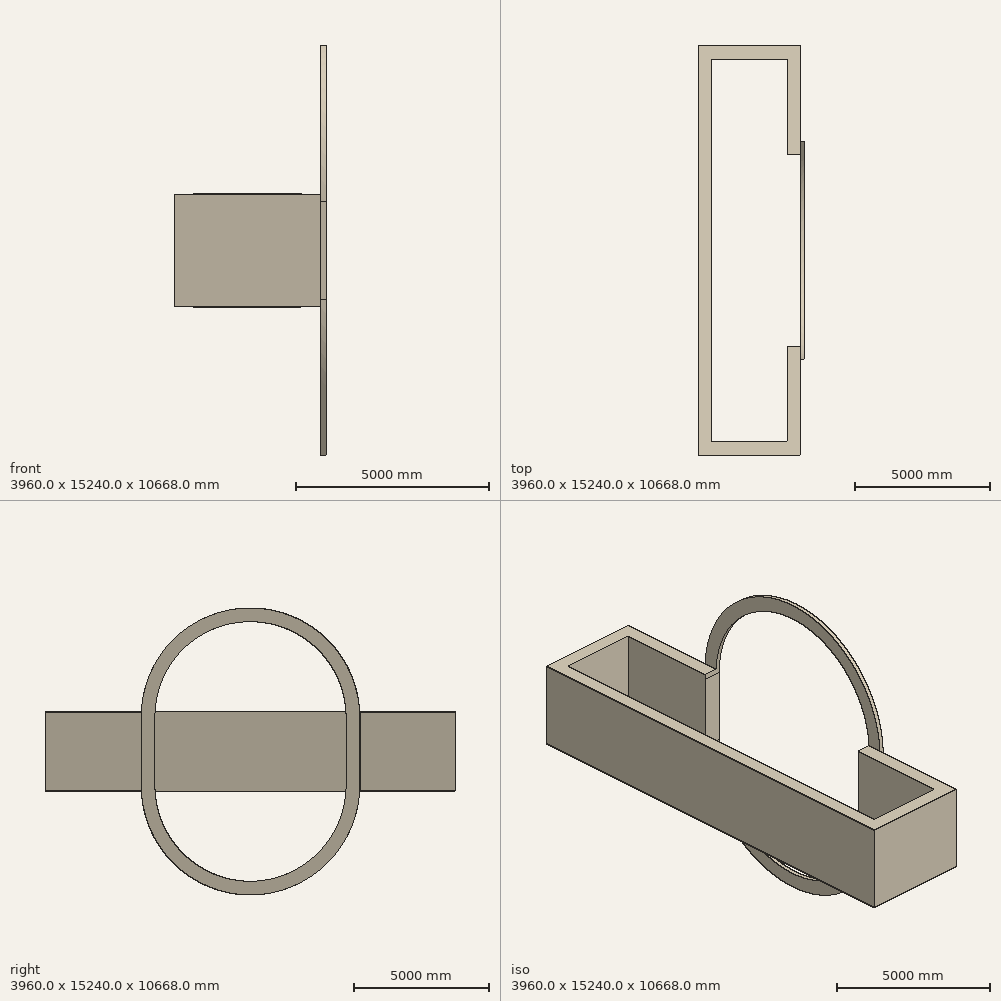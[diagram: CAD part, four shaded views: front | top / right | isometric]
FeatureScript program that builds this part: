
annotation { "Feature Type Name" : "Feature", "Feature Type Description" : "" }
export const myFeature = defineFeature(function(context is Context, id is Id, definition is map)
    precondition{}
    {
        {
            assignVariable(context, id + "F0", {"name" : "H", "anyValue" : 200});
        }
        {
            assignVariable(context, id + "F1", {"name" : "W", "anyValue" : 150});
        }
        {
            assignVariable(context, id + "F2", {"name" : "s", "anyValue" : 20});
        }
        {
            var Q0;
            Q0=qCreatedBy(makeId("Top.planeOp"),FACE);
            var sketch = newSketch(context, id + "F3", { "sketchPlane" : qUnion([Q0])});
            skLineSegment(sketch, "E0.bottom", {"start": v(1905, 7620) * mm, "end": v(-1905, 7620) * mm});
            skLineSegment(sketch, "E0.top", {"start": v(1905, -7620) * mm, "end": v(-1905, -7620) * mm});
            skLineSegment(sketch, "E0.left", {"start": v(1905, 7620) * mm, "end": v(1905, -7620) * mm});
            skLineSegment(sketch, "E0.right", {"start": v(-1905, 7620) * mm, "end": v(-1905, -7620) * mm});
            skLineSegment(sketch, "E1.bottom", {"start": v(1397, 7112) * mm, "end": v(-1397, 7112) * mm});
            skLineSegment(sketch, "E1.top", {"start": v(1397, -7112) * mm, "end": v(-1397, -7112) * mm});
            skLineSegment(sketch, "E1.left", {"start": v(1397, 7112) * mm, "end": v(1397, -7112) * mm});
            skLineSegment(sketch, "E1.right", {"start": v(-1397, 7112) * mm, "end": v(-1397, -7112) * mm});
            skPoint(sketch, "E1.middle", {"position": v(0, 0) * mm});
            skSolve(sketch);
        }
        {
            var Q0;
            Q0 = qSketchRegion(id + "F3", true);
            extrude(context, id + "F4", {"entities" : qUnion([Q0]), "depth" : (getVariable(context, 'H')) * mm});
        }
        {
            var Q0;
            Q0=makeQuery(id+"F4.opExtrude","SWEPT_FACE",FACE,{"disambiguationData":[OSD([sQuery(id+"F3.wireOp",EDGE,"E0.left")])]});
            var sketch = newSketch(context, id + "F5", { "sketchPlane" : qUnion([Q0])});
            skArc(sketch, "E2", {"start": v(4064, 0) * mm, "mid": v(0, 4064) * mm, "end": v(-4064, 0) * mm});
            skLineSegment(sketch, "E3", {"start": v(-4064, 0) * mm, "end": v(4064, 0) * mm});
            skArc(sketch, "E4.0", {"start": v(3556, 0) * mm, "mid": v(0, 3556) * mm, "end": v(-3556, 0) * mm});
            skSolve(sketch);
        }
        {
            var Q0;
            {var subQ0=sQuery(id+"F5.wireOp",EDGE,"E2");Q0=makeQuery(id+"F5.imprint","IMPRINT",FACE,{"disambiguationData":[TD([[makeQuery(id+"F5.imprint","IMPRINT",EDGE,{"derivedFrom":subQ0}),1.0]])]});}
            extrude(context, id + "F6", {"entities" : qUnion([Q0]), "operationType" : NewBodyOperationType.ADD, "depth" : (getVariable(context, 'W')) * mm});
        }
        {
            var Q0;
            {var subQ0=sQuery(id+"F3.wireOp",EDGE,"E0.left");var subQ5=makeQuery(id+"F4.opExtrude","SWEPT_FACE",FACE,{"disambiguationData":[OSD([subQ0])]});var subQ6=sQuery(id+"F5.wireOp",EDGE,"E4.0");Q0=makeQuery(id+"F6.boolean.opBoolean","SPLIT",FACE,{"disambiguationData":[TD([makeQuery(id+"F6.opExtrude","SWEPT_FACE",FACE,{"disambiguationData":[OSD([subQ6])]})])],"derivedFrom":subQ5});}
            var Q1;
            Q1=makeQuery(id+"F4.opExtrude","SWEPT_FACE",FACE,{"disambiguationData":[OSD([sQuery(id+"F3.wireOp",EDGE,"E1.left")])]});
            extrude(context, id + "F7", {"entities" : qUnion([Q0]), "operationType" : NewBodyOperationType.REMOVE, "endBound" : BoundingType.UP_TO_SURFACE, "oppositeDirection" : true, "endBoundEntityFace" : qUnion([Q1]), "depth" : 1473.2 * mm});
        }
        {
            var Q0;
            {var subQ0=sQuery(id+"F5.wireOp",EDGE,"E3");var subQ2=sQuery(id+"F3.wireOp",EDGE,"E0.left");var subQ4=sQuery(id+"F3.wireOp",EDGE,"E0.top");var subQ5=sQuery(id+"F5.wireOp",EDGE,"E4.0");var subQ6=sQuery(id+"F3.wireOp",EDGE,"E0.bottom");Q0=makeQuery(id+"F6.boolean.opBoolean","MERGE",FACE,{"derivedFrom":[makeQuery(id+"F4.opExtrude","CAP_FACE",FACE,{"disambiguationData":[OSD([subQ6,subQ4,subQ2,sQuery(id+"F3.wireOp",EDGE,"E0.right"),sQuery(id+"F3.wireOp",EDGE,"E1.bottom"),sQuery(id+"F3.wireOp",EDGE,"E1.top"),sQuery(id+"F3.wireOp",EDGE,"E1.left"),sQuery(id+"F3.wireOp",EDGE,"E1.right")])],"isStart":true}),makeQuery(id+"F6.opExtrude","SWEPT_FACE",FACE,{"disambiguationData":[OSD([subQ0]),TDD([makeQuery(id+"F5.imprint","IMPRINT",EDGE,{"disambiguationData":[TD([[makeQuery(id+"F5.imprint","INTERSECT",VERTEX,{"disambiguationData":[OD(0.0)],"derivedFrom":[subQ0,subQ5]}),1.0]])],"derivedFrom":subQ0})])]}),makeQuery(id+"F6.opExtrude","SWEPT_FACE",FACE,{"disambiguationData":[OSD([subQ0]),TDD([makeQuery(id+"F5.imprint","IMPRINT",EDGE,{"disambiguationData":[TD([[makeQuery(id+"F5.imprint","INTERSECT",VERTEX,{"disambiguationData":[OD(1.0)],"derivedFrom":[subQ0,subQ5]}),-1.0]])],"derivedFrom":subQ0})])]})]});}
            var sketch = newSketch(context, id + "F8", { "sketchPlane" : qUnion([Q0])});
            skLineSegment(sketch, "E5", {"start": v(5715, -4064) * mm, "end": v(5715, -4064) * mm});
            skSolve(sketch);
        }
        {
            var Q0;
            {var subQ4=sQuery(id+"F3.wireOp",EDGE,"E1.bottom");Q0=makeQuery(id+"F8.imprint","IMPRINT",FACE,{"disambiguationData":[TD([[makeQuery(id+"F8.imprint","IMPRINT",EDGE,{"derivedFrom":makeQuery(id+"F4.opExtrude","CAP_EDGE",EDGE,{"disambiguationData":[OSD([subQ4])],"isStart":true})}),1.0]])]});}
            var Q1;
            {var subQ8=sQuery(id+"F3.wireOp",EDGE,"E1.bottom");Q1=makeQuery(id+"F8.imprint","IMPRINT",FACE,{"disambiguationData":[TD([[makeQuery(id+"F8.imprint","IMPRINT",EDGE,{"derivedFrom":makeQuery(id+"F4.opExtrude","CAP_EDGE",EDGE,{"disambiguationData":[OSD([subQ8])],"isStart":true})}),-1.0]])]});}
            extrude(context, id + "F9", {"entities" : qUnion([Q0, Q1]), "operationType" : NewBodyOperationType.ADD, "depth" : 1270 * mm});
        }
        {
            var Q0;
            Q0=makeQuery(id+"F4.opExtrude","CAP_EDGE",EDGE,{"disambiguationData":[OSD([sQuery(id+"F3.wireOp",EDGE,"E0.top")])],"isStart":false});
            var Q1;
            Q1=makeQuery(id+"F4.opExtrude","CAP_EDGE",EDGE,{"disambiguationData":[OSD([sQuery(id+"F3.wireOp",EDGE,"E0.left")])],"isStart":false});
            var Q2;
            Q2=makeQuery(id+"F4.opExtrude","CAP_EDGE",EDGE,{"disambiguationData":[OSD([sQuery(id+"F3.wireOp",EDGE,"E0.bottom")])],"isStart":false});
            var Q3;
            Q3=makeQuery(id+"F4.opExtrude","CAP_EDGE",EDGE,{"disambiguationData":[OSD([sQuery(id+"F3.wireOp",EDGE,"E0.right")])],"isStart":false});
            var Q4;
            Q4=makeQuery(id+"F4.opExtrude","SWEPT_EDGE",EDGE,{"disambiguationData":[OSD([sQuery(id+"F3.wireOp",EDGE,"E0.top"),sQuery(id+"F3.wireOp",EDGE,"E0.left")])]});
            var Q5;
            Q5=makeQuery(id+"F4.opExtrude","SWEPT_EDGE",EDGE,{"disambiguationData":[OSD([sQuery(id+"F3.wireOp",EDGE,"E0.bottom"),sQuery(id+"F3.wireOp",EDGE,"E0.left")])]});
            var Q6;
            Q6=makeQuery(id+"F4.opExtrude","SWEPT_EDGE",EDGE,{"disambiguationData":[OSD([sQuery(id+"F3.wireOp",EDGE,"E0.top"),sQuery(id+"F3.wireOp",EDGE,"E0.right")])]});
            var Q7;
            Q7=makeQuery(id+"F4.opExtrude","SWEPT_EDGE",EDGE,{"disambiguationData":[OSD([sQuery(id+"F3.wireOp",EDGE,"E0.bottom"),sQuery(id+"F3.wireOp",EDGE,"E0.right")])]});
            fillet(context, id + "F10", {"entities" : qUnion([Q0, Q1, Q2, Q3, Q4, Q5, Q6, Q7]), "radius" : (getVariable(context, 's') / 2) * mm, "tangentPropagation" : true, "allowEdgeOverflow" : false});
        }
        {
            var Q0;
            Q0=makeQuery(id+"F6.opExtrude","CAP_EDGE",EDGE,{"disambiguationData":[OSD([sQuery(id+"F5.wireOp",EDGE,"E2")])],"isStart":false});
            cPoint(context, id + "F11", {"entities" : qUnion([Q0]), "parameter" : 0.5});
        }
        {
            var Q0;
            Q0 = qCreatedBy(id + "F11" ,VERTEX);
            var Q1;
            Q1=makeQuery(id+"F9.opExtrude","CAP_FACE",FACE,{"disambiguationData":[OSD([sQuery(id+"F3.wireOp",EDGE,"E0.bottom"),sQuery(id+"F3.wireOp",EDGE,"E0.top"),sQuery(id+"F3.wireOp",EDGE,"E0.left"),sQuery(id+"F3.wireOp",EDGE,"E0.right"),sQuery(id+"F3.wireOp",EDGE,"E1.bottom"),sQuery(id+"F3.wireOp",EDGE,"E1.top"),sQuery(id+"F3.wireOp",EDGE,"E1.left"),sQuery(id+"F3.wireOp",EDGE,"E1.right"),sQuery(id+"F5.wireOp",EDGE,"E2"),sQuery(id+"F5.wireOp",EDGE,"E3"),sQuery(id+"F5.wireOp",EDGE,"E4.0")])],"isStart":false});
            cPlane(context, id + "F12", {"entities" : qUnion([Q0, Q1]), "cplaneType" : CPlaneType.PLANE_POINT, "offset" : 25.4 * mm, "width" : 152.4 * mm, "height" : 152.4 * mm});
        }
        {
            var Q0;
            Q0=qCreatedBy(id+"F12.planeOp",FACE);
            var sketch = newSketch(context, id + "F13", { "sketchPlane" : qUnion([Q0])});
            skLineSegment(sketch, "E6", {"start": v(1905, 0) * mm, "end": v(5715, 0) * mm});
            skPoint(sketch, "E7", {"position": v(3810, 0) * mm});
            skSolve(sketch);
        }
        {
            var Q0;
            Q0=sQuery(id+"F13.wireOp",VERTEX,"E7");
            var Q1;
            Q1=makeQuery(id+"F4.opExtrude","SWEPT_BODY",BODY,{"disambiguationData":[OSD([sQuery(id+"F3.wireOp",EDGE,"E0.bottom"),sQuery(id+"F3.wireOp",EDGE,"E0.top"),sQuery(id+"F3.wireOp",EDGE,"E0.left"),sQuery(id+"F3.wireOp",EDGE,"E0.right"),sQuery(id+"F3.wireOp",EDGE,"E1.bottom"),sQuery(id+"F3.wireOp",EDGE,"E1.top"),sQuery(id+"F3.wireOp",EDGE,"E1.left"),sQuery(id+"F3.wireOp",EDGE,"E1.right")])]});
            hole(context, id + "F14", {"style" : HoleStyle.SIMPLE, "endStyle" : HoleEndStyle.THROUGH, "oppositeDirection" : true, "holeDiameter" : (getVariable(context, 's') * 2) * mm, "isTappedThrough" : true, "tappedDepth" : 12.7 * mm, "tapClearance" : 3, "locations" : qUnion([Q0]), "scope" : qUnion([Q1])});
        }
        {
            var Q0;
            Q0=makeQuery(id+"F4.opExtrude","SWEPT_BODY",BODY,{"disambiguationData":[OSD([sQuery(id+"F3.wireOp",EDGE,"E0.bottom"),sQuery(id+"F3.wireOp",EDGE,"E0.top"),sQuery(id+"F3.wireOp",EDGE,"E0.left"),sQuery(id+"F3.wireOp",EDGE,"E0.right"),sQuery(id+"F3.wireOp",EDGE,"E1.bottom"),sQuery(id+"F3.wireOp",EDGE,"E1.top"),sQuery(id+"F3.wireOp",EDGE,"E1.left"),sQuery(id+"F3.wireOp",EDGE,"E1.right")])]});
            var Q1;
            Q1=makeQuery(id+"F9.opExtrude","CAP_FACE",FACE,{"disambiguationData":[OSD([sQuery(id+"F3.wireOp",EDGE,"E0.bottom"),sQuery(id+"F3.wireOp",EDGE,"E0.top"),sQuery(id+"F3.wireOp",EDGE,"E0.left"),sQuery(id+"F3.wireOp",EDGE,"E0.right"),sQuery(id+"F3.wireOp",EDGE,"E1.bottom"),sQuery(id+"F3.wireOp",EDGE,"E1.top"),sQuery(id+"F3.wireOp",EDGE,"E1.left"),sQuery(id+"F3.wireOp",EDGE,"E1.right"),sQuery(id+"F5.wireOp",EDGE,"E2"),sQuery(id+"F5.wireOp",EDGE,"E3"),sQuery(id+"F5.wireOp",EDGE,"E4.0")])],"isStart":false});
            mirror(context, id + "F15", {"operationType" : NewBodyOperationType.ADD, "entities" : qUnion([Q0]), "mirrorPlane" : qUnion([Q1])});
        }
        {
            var Q0;
            {var subQ0=sQuery(id+"F3.wireOp",EDGE,"E0.left");var subQ1=makeQuery(id+"F4.opExtrude","SWEPT_FACE",FACE,{"disambiguationData":[OSD([subQ0])]});var subQ4=makeQuery(id+"F4.opExtrude","CAP_EDGE",EDGE,{"disambiguationData":[OSD([subQ0])],"isStart":true});var subQ13=sQuery(id+"F3.wireOp",EDGE,"E0.top");var subQ14=sQuery(id+"F3.wireOp",EDGE,"E0.bottom");var subQ16=makeQuery(id+"F4.opExtrude","SWEPT_FACE",FACE,{"disambiguationData":[OSD([subQ13])]});var subQ18=makeQuery(id+"F4.opExtrude","SWEPT_FACE",FACE,{"disambiguationData":[OSD([subQ14])]});var subQ19=makeQuery(id+"F9.boolean.opBoolean","MERGE",FACE,{"derivedFrom":[makeQuery(id+"F6.boolean.opBoolean","SPLIT",FACE,{"disambiguationData":[TD([subQ18])],"derivedFrom":subQ1}),makeQuery(id+"F9.opExtrude","SWEPT_FACE",FACE,{"disambiguationData":[OSD([subQ0]),TDD([makeQuery(id+"F8.imprint","IMPRINT",EDGE,{"derivedFrom":makeQuery(id+"F6.boolean.opBoolean","SPLIT",EDGE,{"disambiguationData":[TD([subQ18])],"derivedFrom":subQ4})})])]}),makeQuery(id+"F9.opExtrude","SWEPT_FACE",FACE,{"disambiguationData":[OSD([subQ0]),TDD([makeQuery(id+"F8.imprint","IMPRINT",EDGE,{"derivedFrom":makeQuery(id+"F6.boolean.opBoolean","SPLIT",EDGE,{"disambiguationData":[TD([subQ16])],"derivedFrom":subQ4})})])]})]});Q0=makeQuery(id+"F15.boolean.opBoolean","MERGE",FACE,{"derivedFrom":[subQ19,makeQuery(id+"F15.opPattern","COPY",FACE,{"derivedFrom":subQ19,"instanceName":"1"})]});}
            fillet(context, id + "F16", {"entities" : qUnion([Q0]), "radius" : (getVariable(context, 's')) * mm, "tangentPropagation" : true, "allowEdgeOverflow" : false});
        }
    });
